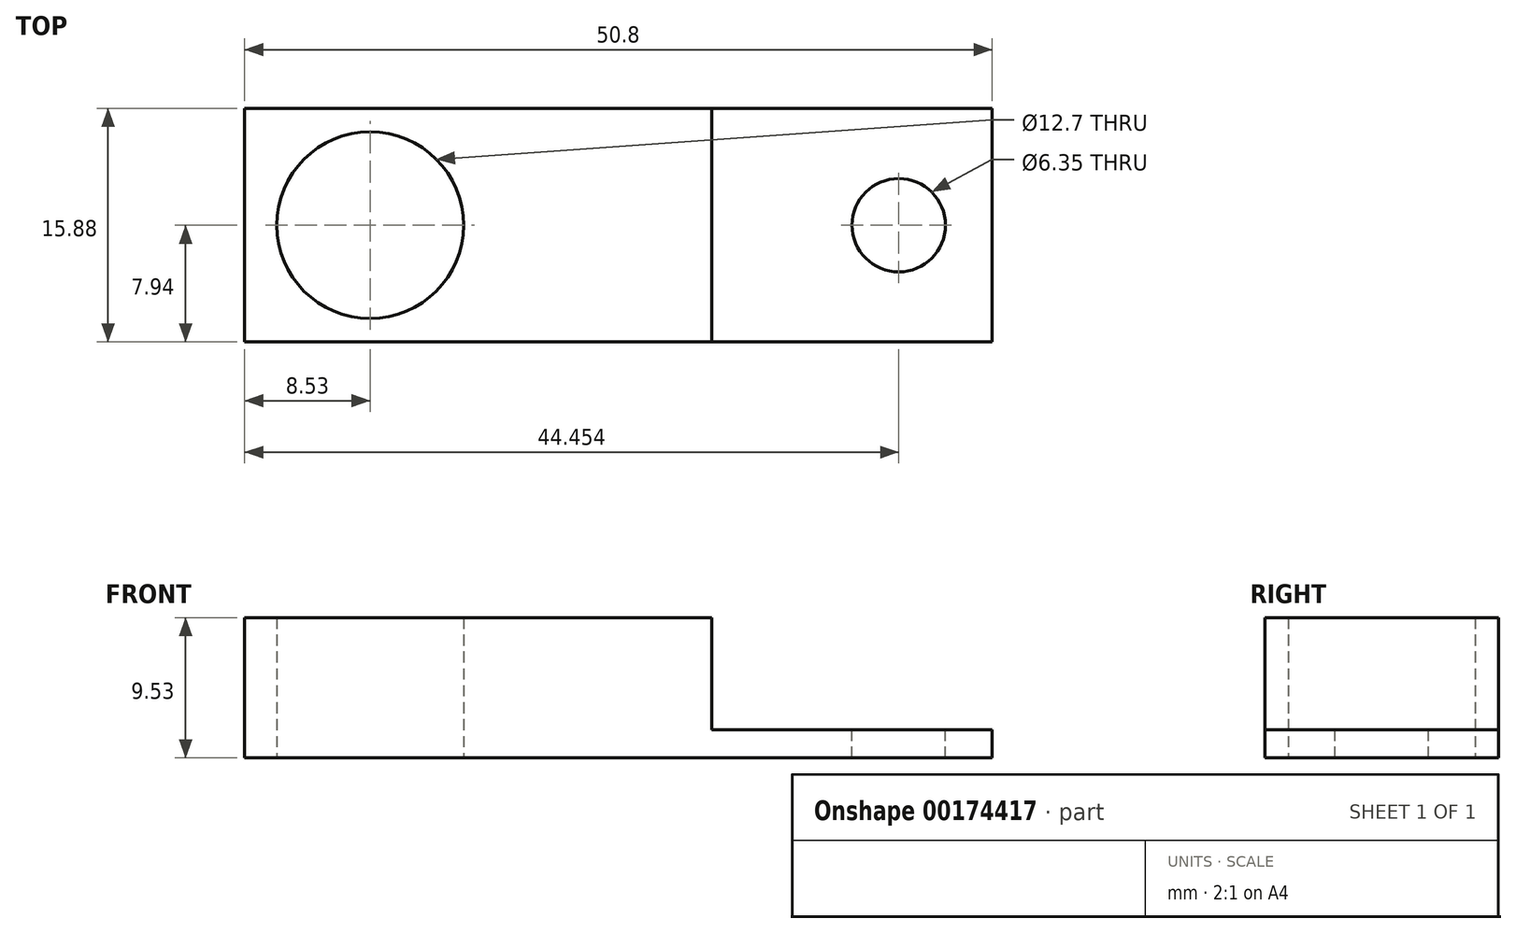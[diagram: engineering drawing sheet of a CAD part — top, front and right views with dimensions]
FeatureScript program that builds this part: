
annotation { "Feature Type Name" : "Feature", "Feature Type Description" : "" }
export const myFeature = defineFeature(function(context is Context, id is Id, definition is map)
    precondition{}
    {
        {
            var Q0;
            Q0=qCreatedBy(makeId("Top.planeOp"),FACE);
            var sketch = newSketch(context, id + "F0", { "sketchPlane" : qUnion([Q0])});
            skCircle(sketch, "E0", {"center": v(0, 0) * mm, "radius": 6.35 * mm});
            skLineSegment(sketch, "E1.bottom", {"start": v(8.53, 7.94) * mm, "end": v(-8.53, 7.94) * mm});
            skLineSegment(sketch, "E1.top", {"start": v(8.53, -7.94) * mm, "end": v(-8.53, -7.94) * mm});
            skLineSegment(sketch, "E1.right", {"start": v(-8.53, 7.94) * mm, "end": v(-8.53, -7.94) * mm});
            skLineSegment(sketch, "E2.bottom", {"start": v(8.53, 7.94) * mm, "end": v(42.27, 7.94) * mm});
            skLineSegment(sketch, "E2.top", {"start": v(8.53, -7.94) * mm, "end": v(42.27, -7.94) * mm});
            skLineSegment(sketch, "E2.right", {"start": v(42.27, 7.94) * mm, "end": v(42.27, -7.94) * mm});
            skSolve(sketch);
        }
        {
            var Q0;
            Q0 = qSketchRegion(id + "F0", true);
            extrude(context, id + "F1", {"entities" : qUnion([Q0]), "depth" : 9.52 * mm});
        }
        {
            var Q0;
            Q0=makeQuery(id+"F1.opExtrude","SWEPT_FACE",FACE,{"disambiguationData":[OSD([sQuery(id+"F0.wireOp",EDGE,"E1.top"),sQuery(id+"F0.wireOp",EDGE,"E2.top")])]});
            var sketch = newSketch(context, id + "F2", { "sketchPlane" : qUnion([Q0])});
            skLineSegment(sketch, "E3.bottom", {"start": v(42.27, 9.53) * mm, "end": v(23.22, 9.53) * mm});
            skLineSegment(sketch, "E3.top", {"start": v(42.27, 1.9) * mm, "end": v(23.22, 1.9) * mm});
            skLineSegment(sketch, "E3.left", {"start": v(42.27, 9.53) * mm, "end": v(42.27, 1.9) * mm});
            skLineSegment(sketch, "E3.right", {"start": v(23.22, 9.53) * mm, "end": v(23.22, 1.9) * mm});
            skSolve(sketch);
        }
        {
            var Q0;
            Q0 = qSketchRegion(id + "F2", true);
            extrude(context, id + "F3", {"entities" : qUnion([Q0]), "operationType" : NewBodyOperationType.REMOVE, "oppositeDirection" : true, "depth" : 25.4 * mm, "offsetDistance" : 25.4 * mm});
        }
        {
            var Q0;
            Q0=makeQuery(id+"F3.boolean.opBoolean","COPY",FACE,{"derivedFrom":makeQuery(id+"F3.opExtrude","SWEPT_FACE",FACE,{"disambiguationData":[OSD([sQuery(id+"F2.wireOp",EDGE,"E3.top")])]})});
            var sketch = newSketch(context, id + "F4", { "sketchPlane" : qUnion([Q0])});
            skCircle(sketch, "E4", {"center": v(35.92, 0) * mm, "radius": 3.18 * mm});
            skSolve(sketch);
        }
        {
            var Q0;
            Q0 = qSketchRegion(id + "F4", true);
            extrude(context, id + "F5", {"entities" : qUnion([Q0]), "operationType" : NewBodyOperationType.REMOVE, "oppositeDirection" : true, "depth" : 25.4 * mm, "offsetDistance" : 25.4 * mm});
        }
    });
